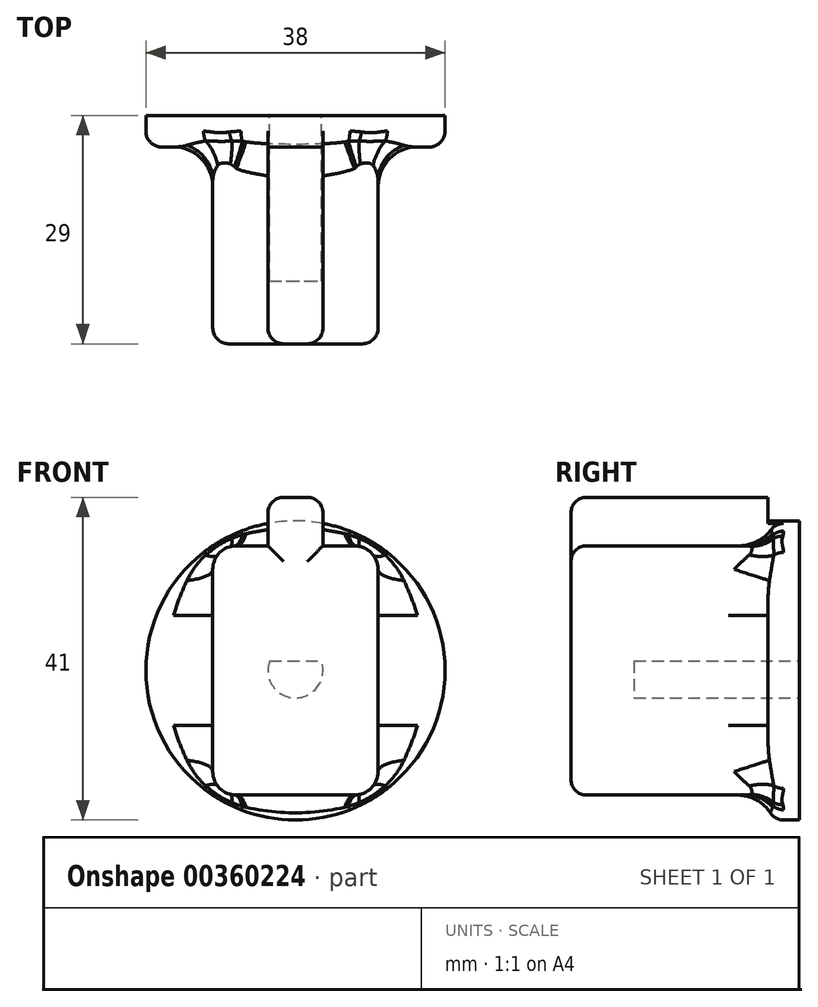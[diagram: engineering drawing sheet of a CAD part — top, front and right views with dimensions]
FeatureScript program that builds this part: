
annotation { "Feature Type Name" : "Feature", "Feature Type Description" : "" }
export const myFeature = defineFeature(function(context is Context, id is Id, definition is map)
    precondition{}
    {
        {
            var Q0;
            Q0=qCreatedBy(makeId("Front.planeOp"),FACE);
            var sketch = newSketch(context, id + "F0", { "sketchPlane" : qUnion([Q0])});
            skCircle(sketch, "E0", {"center": v(0, 0) * mm, "radius": 3.5 * mm});
            skLineSegment(sketch, "E1", {"start": v(-3.29, 1.2) * mm, "end": v(3.29, 1.2) * mm});
            skCircle(sketch, "E2", {"center": v(0, 0) * mm, "radius": 19 * mm});
            skSolve(sketch);
        }
        {
            var Q0;
            Q0=makeQuery(id+"F0.imprint","IMPRINT",FACE,{"disambiguationData":[TD([[makeQuery(id+"F0.imprint","IMPRINT",EDGE,{"derivedFrom":sQuery(id+"F0.wireOp",EDGE,"E2")}),1.0]])]});
            var Q1;
            {var subQ0=sQuery(id+"F0.wireOp",EDGE,"E1");Q1=makeQuery(id+"F0.imprint","IMPRINT",FACE,{"disambiguationData":[TD([[makeQuery(id+"F0.imprint","IMPRINT",EDGE,{"derivedFrom":subQ0}),1.0]])]});}
            var Q2;
            {var subQ0=sQuery(id+"F0.wireOp",EDGE,"E1");Q2=makeQuery(id+"F0.imprint","IMPRINT",FACE,{"disambiguationData":[TD([[makeQuery(id+"F0.imprint","IMPRINT",EDGE,{"derivedFrom":subQ0}),-1.0]])]});}
            extrude(context, id + "F1", {"entities" : qUnion([Q0, Q1, Q2]), "depth" : 4 * mm});
        }
        {
            var Q0;
            Q0=makeQuery(id+"F1.opExtrude","CAP_FACE",FACE,{"disambiguationData":[OSD([sQuery(id+"F0.wireOp",EDGE,"E0"),sQuery(id+"F0.wireOp",EDGE,"E1"),sQuery(id+"F0.wireOp",EDGE,"E2")])],"isStart":false});
            var sketch = newSketch(context, id + "F2", { "sketchPlane" : qUnion([Q0])});
            skLineSegment(sketch, "E3.bottom", {"start": v(10.5, -15.84) * mm, "end": v(-10.5, -15.84) * mm});
            skLineSegment(sketch, "E3.top", {"start": v(10.5, 15.84) * mm, "end": v(-10.5, 15.84) * mm});
            skLineSegment(sketch, "E3.left", {"start": v(10.5, -15.84) * mm, "end": v(10.5, 15.84) * mm});
            skLineSegment(sketch, "E3.right", {"start": v(-10.5, -15.84) * mm, "end": v(-10.5, 15.84) * mm});
            skLineSegment(sketch, "E4.bottom", {"start": v(3.5, 22) * mm, "end": v(-3.5, 22) * mm});
            skLineSegment(sketch, "E4.top", {"start": v(3.5, 9.67) * mm, "end": v(-3.5, 9.67) * mm});
            skLineSegment(sketch, "E4.left", {"start": v(3.5, 22) * mm, "end": v(3.5, 9.67) * mm});
            skLineSegment(sketch, "E4.right", {"start": v(-3.5, 22) * mm, "end": v(-3.5, 9.67) * mm});
            skPoint(sketch, "E4.middle", {"position": v(0, 15.84) * mm});
            skSolve(sketch);
        }
        {
            var Q0;
            Q0=makeQuery(id+"F2.imprint","IMPRINT",FACE,{"disambiguationData":[TD([[makeQuery(id+"F2.imprint","IMPRINT",EDGE,{"derivedFrom":sQuery(id+"F2.wireOp",EDGE,"E3.bottom")}),-1.0]])]});
            var Q1;
            {var subQ5=sQuery(id+"F2.wireOp",EDGE,"E4.top");Q1=makeQuery(id+"F2.imprint","IMPRINT",FACE,{"disambiguationData":[TD([[makeQuery(id+"F2.imprint","IMPRINT",EDGE,{"derivedFrom":subQ5}),-1.0]])]});}
            var Q2;
            {var subQ0=sQuery(id+"F2.wireOp",EDGE,"E4.bottom");Q2=makeQuery(id+"F2.imprint","IMPRINT",FACE,{"disambiguationData":[TD([[makeQuery(id+"F2.imprint","IMPRINT",EDGE,{"derivedFrom":subQ0}),1.0]])]});}
            var Q3;
            {var subQ0=sQuery(id+"F2.wireOp",EDGE,"E4.left");var subQ1=sQuery(id+"F2.wireOp",EDGE,"E3.top");var subQ2=makeQuery(id+"F2.imprint","INTERSECT",VERTEX,{"derivedFrom":[subQ1,subQ0]});Q3=makeQuery(id+"F2.imprint","IMPRINT",FACE,{"disambiguationData":[TD([[makeQuery(id+"F2.imprint","IMPRINT",EDGE,{"disambiguationData":[TD([[subQ2,-1.0]])],"derivedFrom":subQ1}),-1.0]])]});}
            var Q4;
            Q4=makeQuery(id+"F2.imprint","IMPRINT",FACE,{"disambiguationData":[TD([[makeQuery(id+"F2.imprint","IMPRINT",EDGE,{"derivedFrom":makeQuery(id+"F1.opExtrude","CAP_EDGE",EDGE,{"disambiguationData":[OSD([sQuery(id+"F0.wireOp",EDGE,"E0")])],"isStart":false})}),1.0]])]});
            extrude(context, id + "F3", {"entities" : qUnion([Q0, Q1, Q2, Q3, Q4]), "operationType" : NewBodyOperationType.ADD, "depth" : 25 * mm});
        }
        {
            var Q0;
            Q0=makeQuery(id+"F3.opExtrude","SWEPT_EDGE",EDGE,{"disambiguationData":[OSD([sQuery(id+"F0.wireOp",EDGE,"E2"),sQuery(id+"F2.wireOp",EDGE,"E3.top"),sQuery(id+"F2.wireOp",EDGE,"E3.left")])]});
            var Q1;
            Q1=makeQuery(id+"F3.opExtrude","SWEPT_EDGE",EDGE,{"disambiguationData":[OSD([sQuery(id+"F0.wireOp",EDGE,"E2"),sQuery(id+"F2.wireOp",EDGE,"E3.top"),sQuery(id+"F2.wireOp",EDGE,"E3.right")])]});
            var Q2;
            Q2=makeQuery(id+"F3.opExtrude","SWEPT_EDGE",EDGE,{"disambiguationData":[OSD([sQuery(id+"F0.wireOp",EDGE,"E2"),sQuery(id+"F2.wireOp",EDGE,"E3.bottom"),sQuery(id+"F2.wireOp",EDGE,"E3.right")])]});
            var Q3;
            Q3=makeQuery(id+"F3.opExtrude","SWEPT_EDGE",EDGE,{"disambiguationData":[OSD([sQuery(id+"F0.wireOp",EDGE,"E2"),sQuery(id+"F2.wireOp",EDGE,"E3.bottom"),sQuery(id+"F2.wireOp",EDGE,"E3.left")])]});
            fillet(context, id + "F4", {"entities" : qUnion([Q0, Q1, Q2, Q3]), "radius" : 3 * mm, "allowEdgeOverflow" : false});
        }
        {
            var Q0;
            Q0=makeQuery(id+"F3.opExtrude","CAP_FACE",FACE,{"disambiguationData":[OSD([sQuery(id+"F2.wireOp",EDGE,"E3.bottom"),sQuery(id+"F2.wireOp",EDGE,"E3.top"),sQuery(id+"F2.wireOp",EDGE,"E3.left"),sQuery(id+"F2.wireOp",EDGE,"E3.right"),sQuery(id+"F2.wireOp",EDGE,"E4.bottom"),sQuery(id+"F2.wireOp",EDGE,"E4.left"),sQuery(id+"F2.wireOp",EDGE,"E4.right")])],"isStart":false});
            var Q1;
            Q1=makeQuery(id+"F3.opExtrude","SWEPT_EDGE",EDGE,{"disambiguationData":[OSD([sQuery(id+"F2.wireOp",EDGE,"E4.bottom"),sQuery(id+"F2.wireOp",EDGE,"E4.right")])]});
            var Q2;
            Q2=makeQuery(id+"F3.opExtrude","SWEPT_EDGE",EDGE,{"disambiguationData":[OSD([sQuery(id+"F2.wireOp",EDGE,"E4.bottom"),sQuery(id+"F2.wireOp",EDGE,"E4.left")])]});
            var Q3;
            {var subQ0=sQuery(id+"F0.wireOp",EDGE,"E2");var subQ1=makeQuery(id+"F1.opExtrude","SWEPT_FACE",FACE,{"disambiguationData":[OSD([subQ0])]});var subQ2=makeQuery(id+"F1.opExtrude","CAP_FACE",FACE,{"disambiguationData":[OSD([sQuery(id+"F0.wireOp",EDGE,"E0"),sQuery(id+"F0.wireOp",EDGE,"E1"),subQ0])],"isStart":false});Q3=makeQuery(id+"F3.boolean.opBoolean","SPLIT",EDGE,{"disambiguationData":[topologyDisambiguationEdgeConnected([subQ2,subQ1]),TD([subQ2,subQ1,makeQuery(id+"F3.opExtrude","SWEPT_FACE",FACE,{"disambiguationData":[OSD([sQuery(id+"F2.wireOp",EDGE,"E3.bottom")])]}),makeQuery(id+"F3.opExtrude","SWEPT_FACE",FACE,{"disambiguationData":[OSD([sQuery(id+"F2.wireOp",EDGE,"E3.left")])]}),makeQuery(id+"F3.opExtrude","SWEPT_FACE",FACE,{"disambiguationData":[OSD([sQuery(id+"F2.wireOp",EDGE,"E3.right")])]})])],"derivedFrom":makeQuery(id+"F1.opExtrude","CAP_EDGE",EDGE,{"disambiguationData":[OSD([subQ0])],"isStart":false})});}
            fillet(context, id + "F5", {"entities" : qUnion([Q0, Q1, Q2, Q3]), "radius" : 2 * mm, "tangentPropagation" : true, "allowEdgeOverflow" : false});
        }
        {
            var Q0;
            Q0=makeQuery(id+"F3.opExtrude","CAP_EDGE",EDGE,{"disambiguationData":[OSD([sQuery(id+"F2.wireOp",EDGE,"E3.right")])],"isStart":true});
            fillet(context, id + "F6", {"entities" : qUnion([Q0]), "radius" : 5 * mm, "tangentPropagation" : true, "allowEdgeOverflow" : false});
        }
        {
            var Q0;
            {var subQ0=sQuery(id+"F0.wireOp",EDGE,"E1");Q0=makeQuery(id+"F0.imprint","IMPRINT",FACE,{"disambiguationData":[TD([[makeQuery(id+"F0.imprint","IMPRINT",EDGE,{"derivedFrom":subQ0}),-1.0]])]});}
            extrude(context, id + "F7", {"entities" : qUnion([Q0]), "operationType" : NewBodyOperationType.REMOVE, "depth" : 21 * mm});
        }
    });
